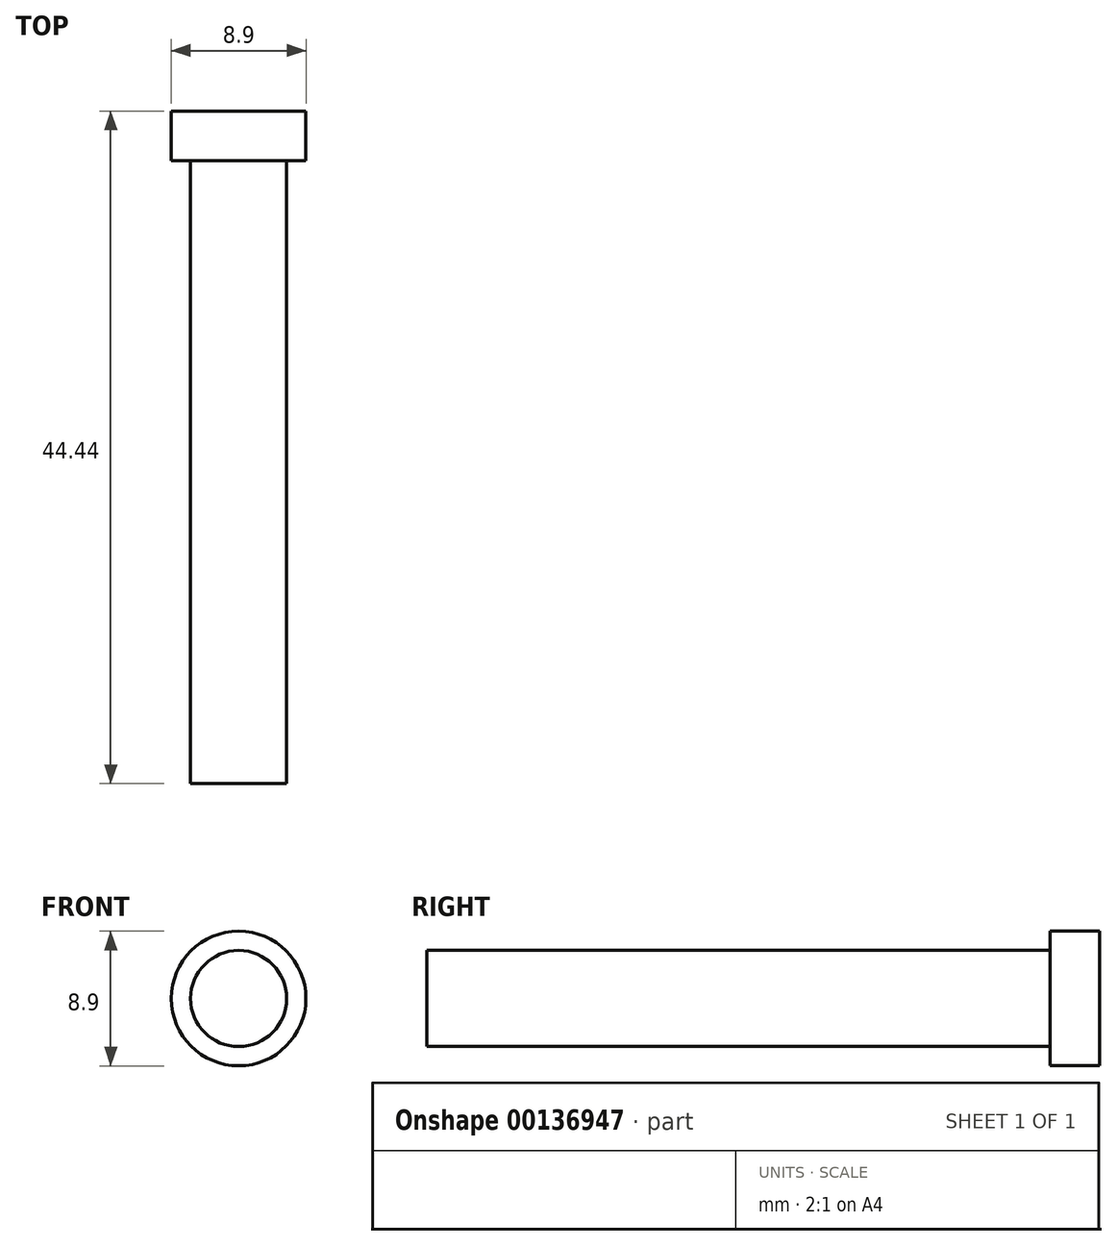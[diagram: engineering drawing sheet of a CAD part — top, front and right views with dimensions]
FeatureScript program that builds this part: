
annotation { "Feature Type Name" : "Feature", "Feature Type Description" : "" }
export const myFeature = defineFeature(function(context is Context, id is Id, definition is map)
    precondition{}
    {
        {
            var Q0;
            Q0=qCreatedBy(makeId("Front.planeOp"),FACE);
            var sketch = newSketch(context, id + "F0", { "sketchPlane" : qUnion([Q0])});
            skCircle(sketch, "E0", {"center": v(0, 0) * mm, "radius": 3.18 * mm});
            skSolve(sketch);
        }
        {
            var Q0;
            Q0=makeQuery(id+"F0.imprint","IMPRINT",FACE,{"disambiguationData":[TD([[makeQuery(id+"F0.imprint","IMPRINT",EDGE,{"derivedFrom":sQuery(id+"F0.wireOp",EDGE,"E0")}),1.0]])]});
            extrude(context, id + "F1", {"entities" : qUnion([Q0]), "depth" : 41.15 * mm});
        }
        {
            var Q0;
            Q0=qCreatedBy(makeId("Front.planeOp"),FACE);
            var sketch = newSketch(context, id + "F2", { "sketchPlane" : qUnion([Q0])});
            skCircle(sketch, "E1", {"center": v(0, 0) * mm, "radius": 4.45 * mm});
            skSolve(sketch);
        }
        {
            var Q0;
            Q0 = qSketchRegion(id + "F2", true);
            extrude(context, id + "F3", {"entities" : qUnion([Q0]), "operationType" : NewBodyOperationType.ADD, "oppositeDirection" : true, "depth" : 3.3 * mm});
        }
    });
